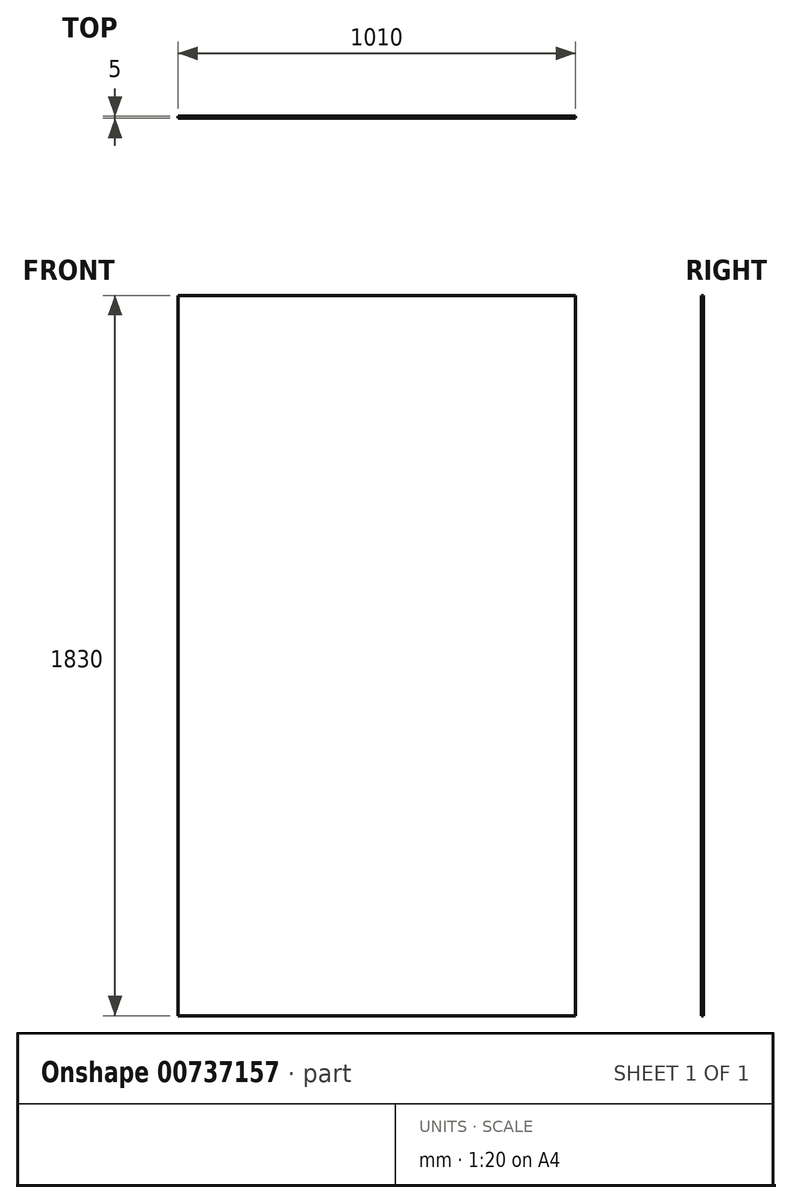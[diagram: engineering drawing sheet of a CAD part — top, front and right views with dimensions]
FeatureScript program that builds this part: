
annotation { "Feature Type Name" : "Feature", "Feature Type Description" : "" }
export const myFeature = defineFeature(function(context is Context, id is Id, definition is map)
    precondition{}
    {
        {
            var Q0;
            Q0=qCreatedBy(makeId("Front.planeOp"),FACE);
            var sketch = newSketch(context, id + "F0", { "sketchPlane" : qUnion([Q0])});
            skLineSegment(sketch, "E0.bottom", {"start": v(505, -915) * mm, "end": v(-505, -915) * mm});
            skLineSegment(sketch, "E0.top", {"start": v(505, 915) * mm, "end": v(-505, 915) * mm});
            skLineSegment(sketch, "E0.left", {"start": v(505, -915) * mm, "end": v(505, 915) * mm});
            skLineSegment(sketch, "E0.right", {"start": v(-505, -915) * mm, "end": v(-505, 915) * mm});
            skPoint(sketch, "E0.middle", {"position": v(0, 0) * mm});
            skSolve(sketch);
        }
        {
            var Q0;
            Q0 = qSketchRegion(id + "F0", true);
            extrude(context, id + "F1", {"entities" : qUnion([Q0]), "depth" : 5 * mm, "offsetDistance" : 25 * mm});
        }
    });
